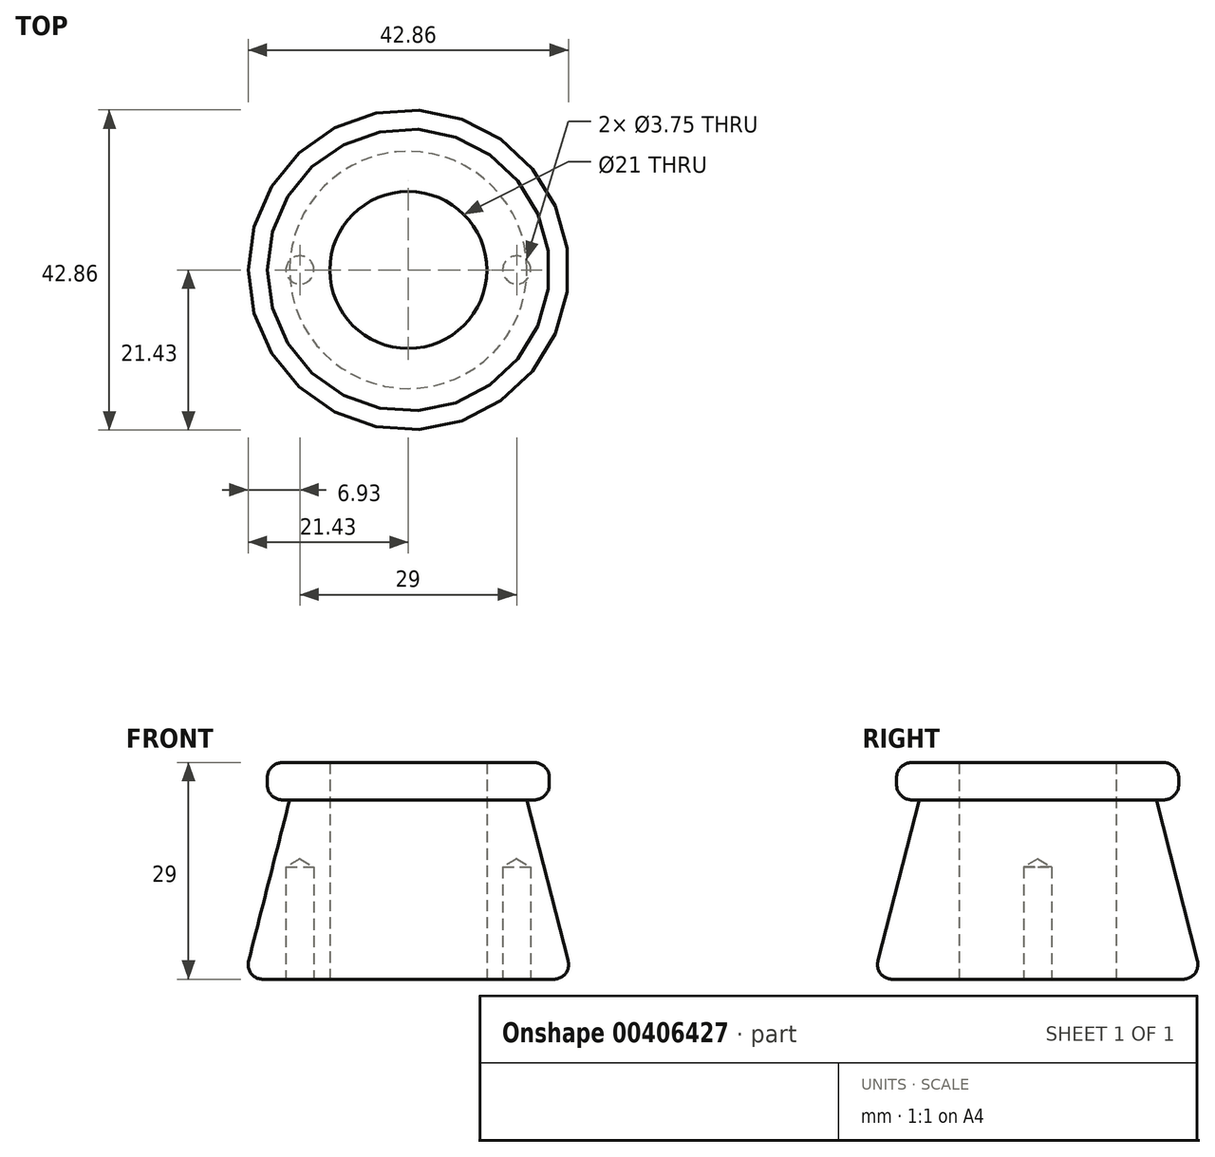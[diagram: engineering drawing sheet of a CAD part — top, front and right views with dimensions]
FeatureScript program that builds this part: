
annotation { "Feature Type Name" : "Feature", "Feature Type Description" : "" }
export const myFeature = defineFeature(function(context is Context, id is Id, definition is map)
    precondition{}
    {
        {
            var Q0;
            Q0=qCreatedBy(makeId("Front.planeOp"),FACE);
            var sketch = newSketch(context, id + "F0", { "sketchPlane" : qUnion([Q0])});
            skLineSegment(sketch, "E0", {"start": v(-10.5, 0) * mm, "end": v(-10.5, 29) * mm});
            skLineSegment(sketch, "E1", {"start": v(-10.5, 29) * mm, "end": v(-18.87, 29) * mm});
            skLineSegment(sketch, "E2", {"start": v(-18.87, 29) * mm, "end": v(-18.87, 24) * mm});
            skLineSegment(sketch, "E3", {"start": v(-18.87, 24) * mm, "end": v(-15.87, 24) * mm});
            skLineSegment(sketch, "E4", {"start": v(-15.87, 24) * mm, "end": v(-22, 0) * mm});
            skLineSegment(sketch, "E5", {"start": v(-22, 0) * mm, "end": v(-10.5, 0) * mm});
            skLineSegment(sketch, "E6", {"start": v(0, 0) * mm, "end": v(0, 29) * mm, "construction": true});
            skSolve(sketch);
        }
        {
            var Q0;
            Q0=makeQuery(id+"F0.imprint","IMPRINT",FACE,{"disambiguationData":[TD([[makeQuery(id+"F0.imprint","IMPRINT",EDGE,{"derivedFrom":sQuery(id+"F0.wireOp",EDGE,"E0")}),1.0]])]});
            var Q1;
            Q1=sQuery(id+"F0.wireOp",EDGE,"E6");
            revolve(context, id + "F1", {"entities" : qUnion([Q0]), "axis" : qUnion([Q1]), "revolveType" : RevolveType.FULL});
        }
        {
            var Q0;
            Q0=makeQuery(id+"F1.opRevolve","SWEPT_EDGE",EDGE,{"disambiguationData":[OSD([sQuery(id+"F0.wireOp",EDGE,"E4"),sQuery(id+"F0.wireOp",EDGE,"E5")])]});
            var Q1;
            Q1=makeQuery(id+"F1.opRevolve","SWEPT_EDGE",EDGE,{"disambiguationData":[OSD([sQuery(id+"F0.wireOp",EDGE,"E1"),sQuery(id+"F0.wireOp",EDGE,"E2")])]});
            var Q2;
            Q2=makeQuery(id+"F1.opRevolve","SWEPT_EDGE",EDGE,{"disambiguationData":[OSD([sQuery(id+"F0.wireOp",EDGE,"E4"),sQuery(id+"F0.wireOp",EDGE,"E5")])]});
            var Q3;
            Q3=makeQuery(id+"F1.opRevolve","SWEPT_EDGE",EDGE,{"disambiguationData":[OSD([sQuery(id+"F0.wireOp",EDGE,"E2"),sQuery(id+"F0.wireOp",EDGE,"E3")])]});
            fillet(context, id + "F2", {"entities" : qUnion([Q0, Q1, Q2, Q3]), "radius" : 2 * mm, "tangentPropagation" : true, "rho" : 0.4, "crossSection" : FilletCrossSection.CONIC, "allowEdgeOverflow" : false});
        }
        {
            var Q0;
            Q0=makeQuery(id+"F1.opRevolve","SWEPT_FACE",FACE,{"disambiguationData":[OSD([sQuery(id+"F0.wireOp",EDGE,"E5")])]});
            var sketch = newSketch(context, id + "F3", { "sketchPlane" : qUnion([Q0])});
            skLineSegment(sketch, "E7", {"start": v(-14.5, 0) * mm, "end": v(14.5, 0) * mm, "construction": true});
            skSolve(sketch);
        }
        {
            var Q0;
            Q0=sQuery(id+"F3.wireOp",VERTEX,"E7.start");
            var Q1;
            Q1=sQuery(id+"F3.wireOp",VERTEX,"E7.end");
            var Q2;
            Q2=makeQuery(id+"F1.opRevolve","SWEPT_BODY",BODY,{"disambiguationData":[OSD([sQuery(id+"F0.wireOp",EDGE,"E0"),sQuery(id+"F0.wireOp",EDGE,"E1"),sQuery(id+"F0.wireOp",EDGE,"E2"),sQuery(id+"F0.wireOp",EDGE,"E3"),sQuery(id+"F0.wireOp",EDGE,"qPnWj9SD-eYo5-YZIC-HoWk-tVNfriIZjeKu"),sQuery(id+"F0.wireOp",EDGE,"xlKEw2gX-onh0-BwSc-uQZH-ZjNXgl5m2rjK"),sQuery(id+"F0.wireOp",EDGE,"E4"),sQuery(id+"F0.wireOp",EDGE,"E5")])]});
            hole(context, id + "F4", {"style" : HoleStyle.SIMPLE, "endStyle" : HoleEndStyle.BLIND, "holeDiameter" : 3.75 * mm, "holeDepth" : 15 * mm, "isTappedThrough" : true, "tappedDepth" : 46.25 * mm, "tapClearance" : 3, "locations" : qUnion([Q0, Q1]), "scope" : qUnion([Q2])});
        }
    });
